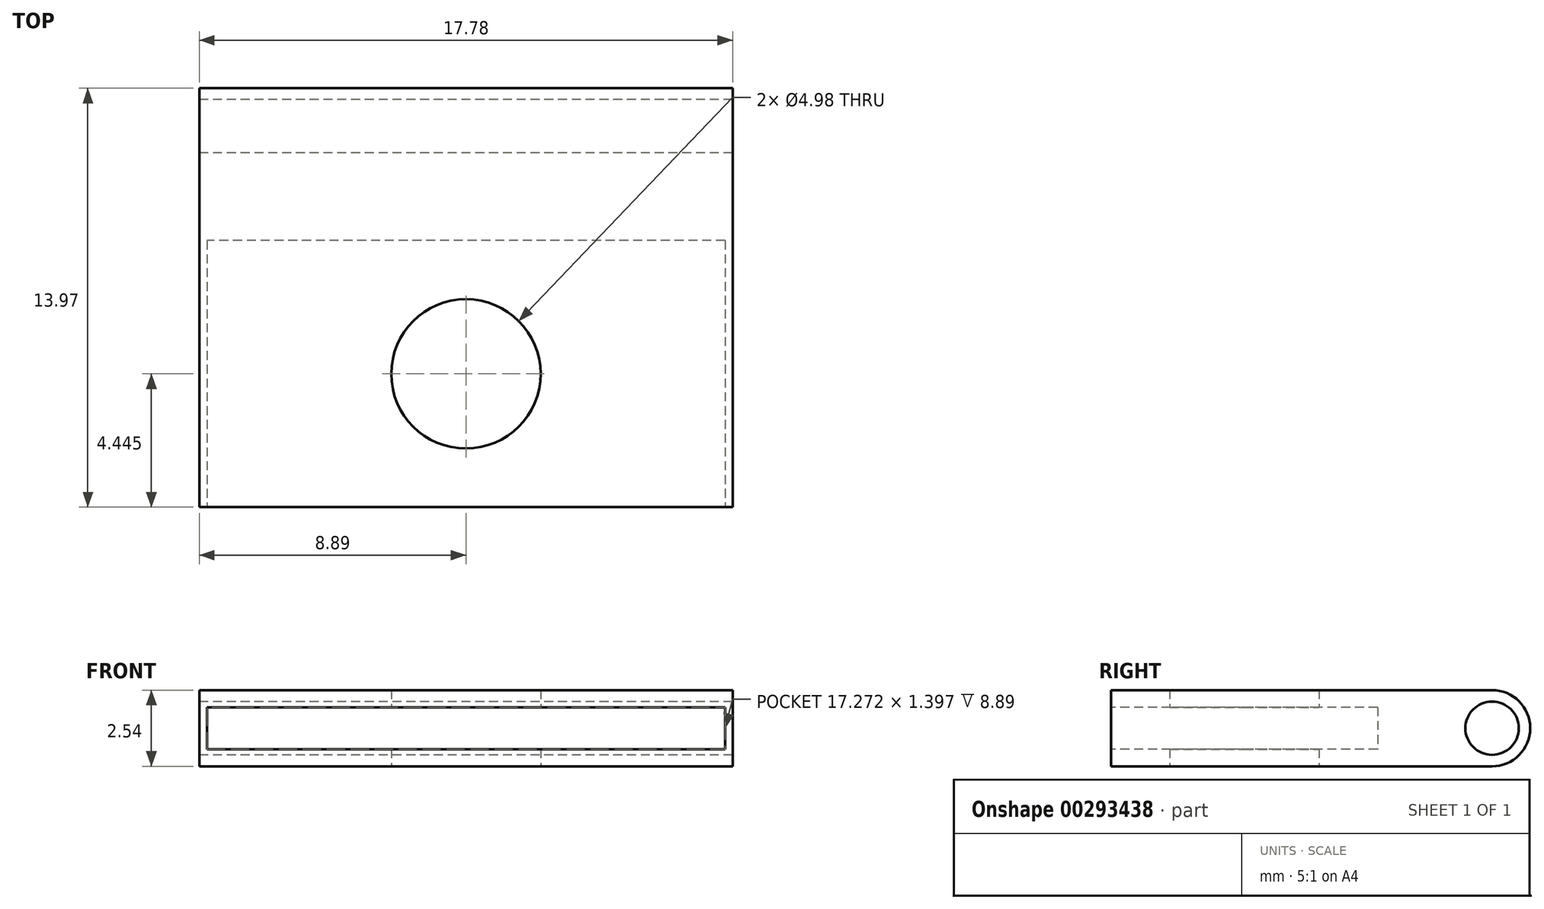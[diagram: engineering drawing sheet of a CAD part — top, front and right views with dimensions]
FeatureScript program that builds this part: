
annotation { "Feature Type Name" : "Feature", "Feature Type Description" : "" }
export const myFeature = defineFeature(function(context is Context, id is Id, definition is map)
    precondition{}
    {
        {
            var Q0;
            Q0=qCreatedBy(makeId("Top.planeOp"),FACE);
            var sketch = newSketch(context, id + "F0", { "sketchPlane" : qUnion([Q0])});
            skLineSegment(sketch, "E0.bottom", {"start": v(0, 0) * mm, "end": v(17.78, 0) * mm});
            skLineSegment(sketch, "E0.top", {"start": v(0, 12.7) * mm, "end": v(17.78, 12.7) * mm});
            skLineSegment(sketch, "E0.left", {"start": v(0, 0) * mm, "end": v(0, 12.7) * mm});
            skLineSegment(sketch, "E0.right", {"start": v(17.78, 0) * mm, "end": v(17.78, 12.7) * mm});
            skCircle(sketch, "E1", {"center": v(8.9, 4.45) * mm, "radius": 2.49 * mm});
            skSolve(sketch);
        }
        {
            var Q0;
            Q0=makeQuery(id+"F0.imprint","IMPRINT",FACE,{"disambiguationData":[TD([[makeQuery(id+"F0.imprint","IMPRINT",EDGE,{"derivedFrom":sQuery(id+"F0.wireOp",EDGE,"E0.bottom")}),1.0]])]});
            extrude(context, id + "F1", {"entities" : qUnion([Q0]), "depth" : 2.54 * mm});
        }
        {
            var Q0;
            Q0=makeQuery(id+"F1.opExtrude","SWEPT_FACE",FACE,{"disambiguationData":[OSD([sQuery(id+"F0.wireOp",EDGE,"E0.bottom")])]});
            var sketch = newSketch(context, id + "F2", { "sketchPlane" : qUnion([Q0])});
            skLineSegment(sketch, "E2.bottom", {"start": v(17.53, 1.97) * mm, "end": v(0.25, 1.97) * mm});
            skLineSegment(sketch, "E2.top", {"start": v(17.53, 0.57) * mm, "end": v(0.25, 0.57) * mm});
            skLineSegment(sketch, "E2.left", {"start": v(17.53, 1.97) * mm, "end": v(17.53, 0.57) * mm});
            skLineSegment(sketch, "E2.right", {"start": v(0.25, 1.97) * mm, "end": v(0.25, 0.57) * mm});
            skPoint(sketch, "E2.middle", {"position": v(8.9, 1.27) * mm});
            skSolve(sketch);
        }
        {
            var Q0;
            Q0=makeQuery(id+"F2.imprint","IMPRINT",FACE,{"disambiguationData":[TD([[makeQuery(id+"F2.imprint","IMPRINT",EDGE,{"derivedFrom":sQuery(id+"F2.wireOp",EDGE,"E2.bottom")}),1.0]])]});
            extrude(context, id + "F3", {"entities" : qUnion([Q0]), "operationType" : NewBodyOperationType.REMOVE, "oppositeDirection" : true, "depth" : 8.9 * mm});
        }
        {
            var Q0;
            Q0=makeQuery(id+"F1.opExtrude","SWEPT_FACE",FACE,{"disambiguationData":[OSD([sQuery(id+"F0.wireOp",EDGE,"E0.left")])]});
            var sketch = newSketch(context, id + "F4", { "sketchPlane" : qUnion([Q0])});
            skCircle(sketch, "E3", {"center": v(-12.7, 1.27) * mm, "radius": 1.27 * mm});
            skPoint(sketch, "E4", {"position": v(-12.7, 2.54) * mm});
            skPoint(sketch, "E5", {"position": v(-12.7, 0) * mm});
            skCircle(sketch, "E6", {"center": v(-12.7, 1.27) * mm, "radius": 0.89 * mm});
            skSolve(sketch);
        }
        {
            var Q0;
            {var subQ1=sQuery(id+"F0.wireOp",EDGE,"E0.left");var subQ2=makeQuery(id+"F1.opExtrude","SWEPT_EDGE",EDGE,{"disambiguationData":[OSD([sQuery(id+"F0.wireOp",EDGE,"E0.top"),subQ1])]});var subQ5=sQuery(id+"F4.wireOp",EDGE,"E6");var subQ6=makeQuery(id+"F4.imprint","INTERSECT",VERTEX,{"disambiguationData":[OD(0.0)],"derivedFrom":[subQ2,subQ5]});Q0=makeQuery(id+"F4.imprint","IMPRINT",FACE,{"disambiguationData":[TD([[makeQuery(id+"F4.imprint","IMPRINT",EDGE,{"disambiguationData":[TD([[subQ6,1.0]])],"derivedFrom":subQ5}),-1.0]])]});}
            extrude(context, id + "F5", {"entities" : qUnion([Q0]), "operationType" : NewBodyOperationType.ADD, "oppositeDirection" : true, "depth" : 17.78 * mm});
        }
        {
            var Q0;
            {var subQ0=sQuery(id+"F4.wireOp",EDGE,"E6");var subQ1=makeQuery(id+"F1.opExtrude","SWEPT_EDGE",EDGE,{"disambiguationData":[OSD([sQuery(id+"F0.wireOp",EDGE,"E0.top"),sQuery(id+"F0.wireOp",EDGE,"E0.left")])]});var subQ2=makeQuery(id+"F4.imprint","INTERSECT",VERTEX,{"disambiguationData":[OD(0.0)],"derivedFrom":[subQ1,subQ0]});Q0=makeQuery(id+"F4.imprint","IMPRINT",FACE,{"disambiguationData":[TD([[makeQuery(id+"F4.imprint","IMPRINT",EDGE,{"disambiguationData":[TD([[subQ2,-1.0]])],"derivedFrom":subQ0}),1.0]])]});}
            extrude(context, id + "F6", {"entities" : qUnion([Q0]), "operationType" : NewBodyOperationType.REMOVE, "oppositeDirection" : true, "depth" : 25.4 * mm});
        }
    });
